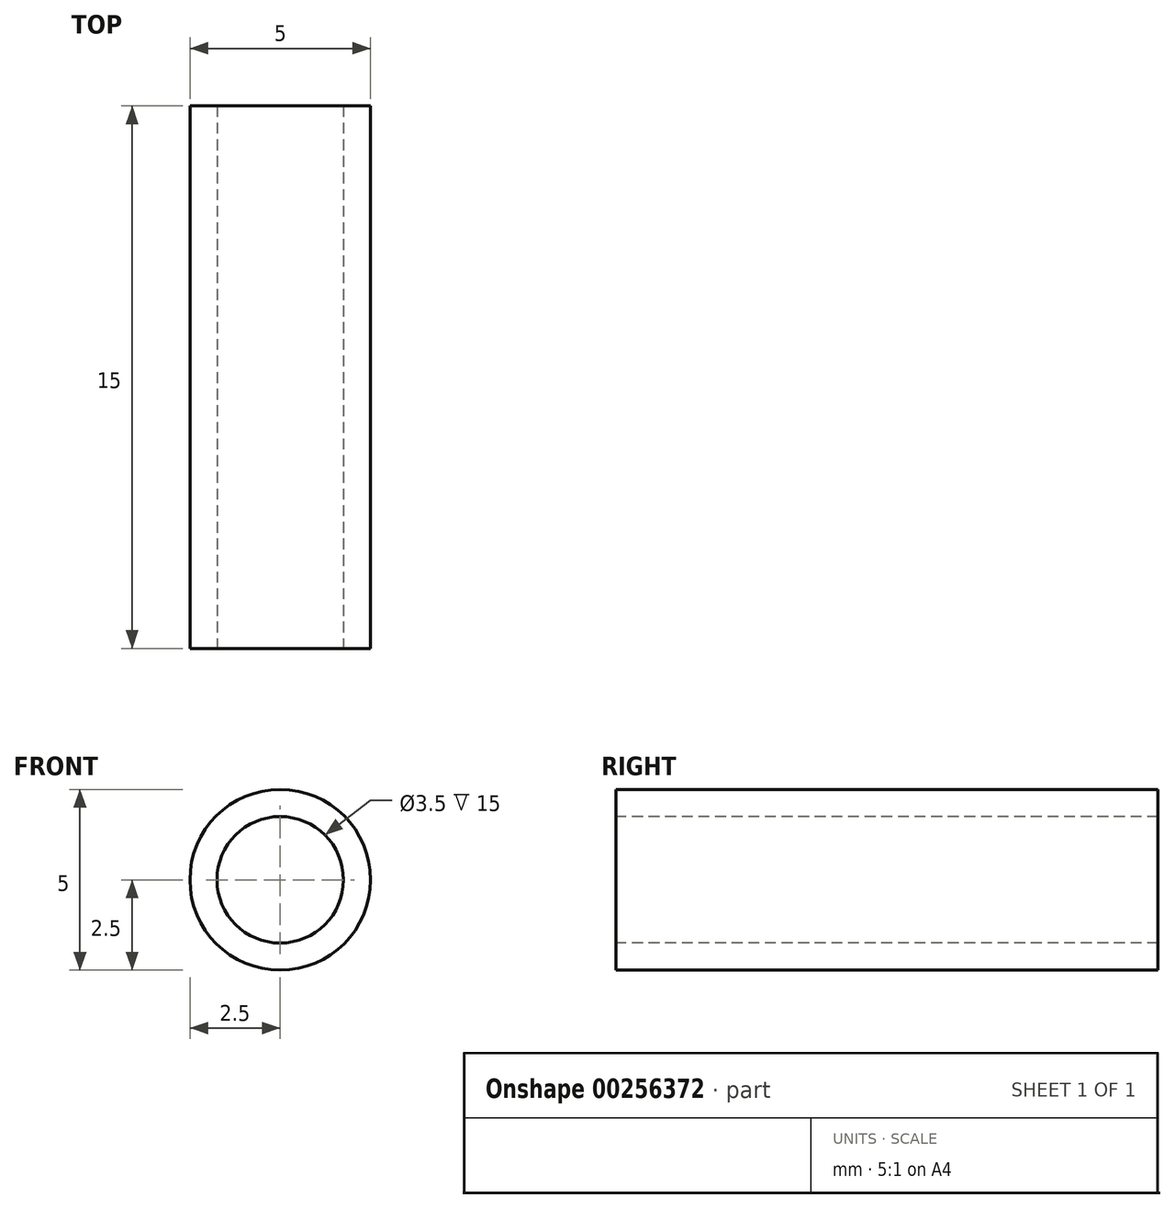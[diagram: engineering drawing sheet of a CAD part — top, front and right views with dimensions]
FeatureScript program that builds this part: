
annotation { "Feature Type Name" : "Feature", "Feature Type Description" : "" }
export const myFeature = defineFeature(function(context is Context, id is Id, definition is map)
    precondition{}
    {
        {
            var Q0;
            Q0=qCreatedBy(makeId("Front.planeOp"),FACE);
            var sketch = newSketch(context, id + "F0", { "sketchPlane" : qUnion([Q0])});
            skCircle(sketch, "E0", {"center": v(0, 0) * mm, "radius": 2.5 * mm});
            skSolve(sketch);
        }
        {
            var Q0;
            Q0 = qSketchRegion(id + "F0", true);
            extrude(context, id + "F1", {"entities" : qUnion([Q0]), "depth" : 15 * mm});
        }
        {
            var Q0;
            Q0=makeQuery(id+"F1.opExtrude","CAP_FACE",FACE,{"disambiguationData":[OSD([sQuery(id+"F0.wireOp",EDGE,"E0")])],"isStart":false});
            var sketch = newSketch(context, id + "F2", { "sketchPlane" : qUnion([Q0])});
            skPoint(sketch, "E1", {"position": v(0, 0) * mm});
            skSolve(sketch);
        }
        {
            var Q0;
            Q0=sQuery(id+"F2.wireOp",VERTEX,"E1");
            var Q1;
            Q1=makeQuery(id+"F1.opExtrude","SWEPT_BODY",BODY,{"disambiguationData":[OSD([sQuery(id+"F0.wireOp",EDGE,"E0")])]});
            hole(context, id + "F3", {"style" : HoleStyle.SIMPLE, "endStyle" : HoleEndStyle.THROUGH, "standardTappedOrClearance" : lookupTablePath({ "standard" : "ISO", "size" : "3.5", "type" : "Drilled" }), "standardBlindInLast" : lookupTablePath({ "standard" : "ISO", "size" : "3.5", "type" : "Drilled" }), "holeDiameter" : 3.5 * mm, "tappedDepth" : 0.64 * mm, "tapClearance" : 3, "locations" : qUnion([Q0]), "scope" : qUnion([Q1])});
        }
    });
